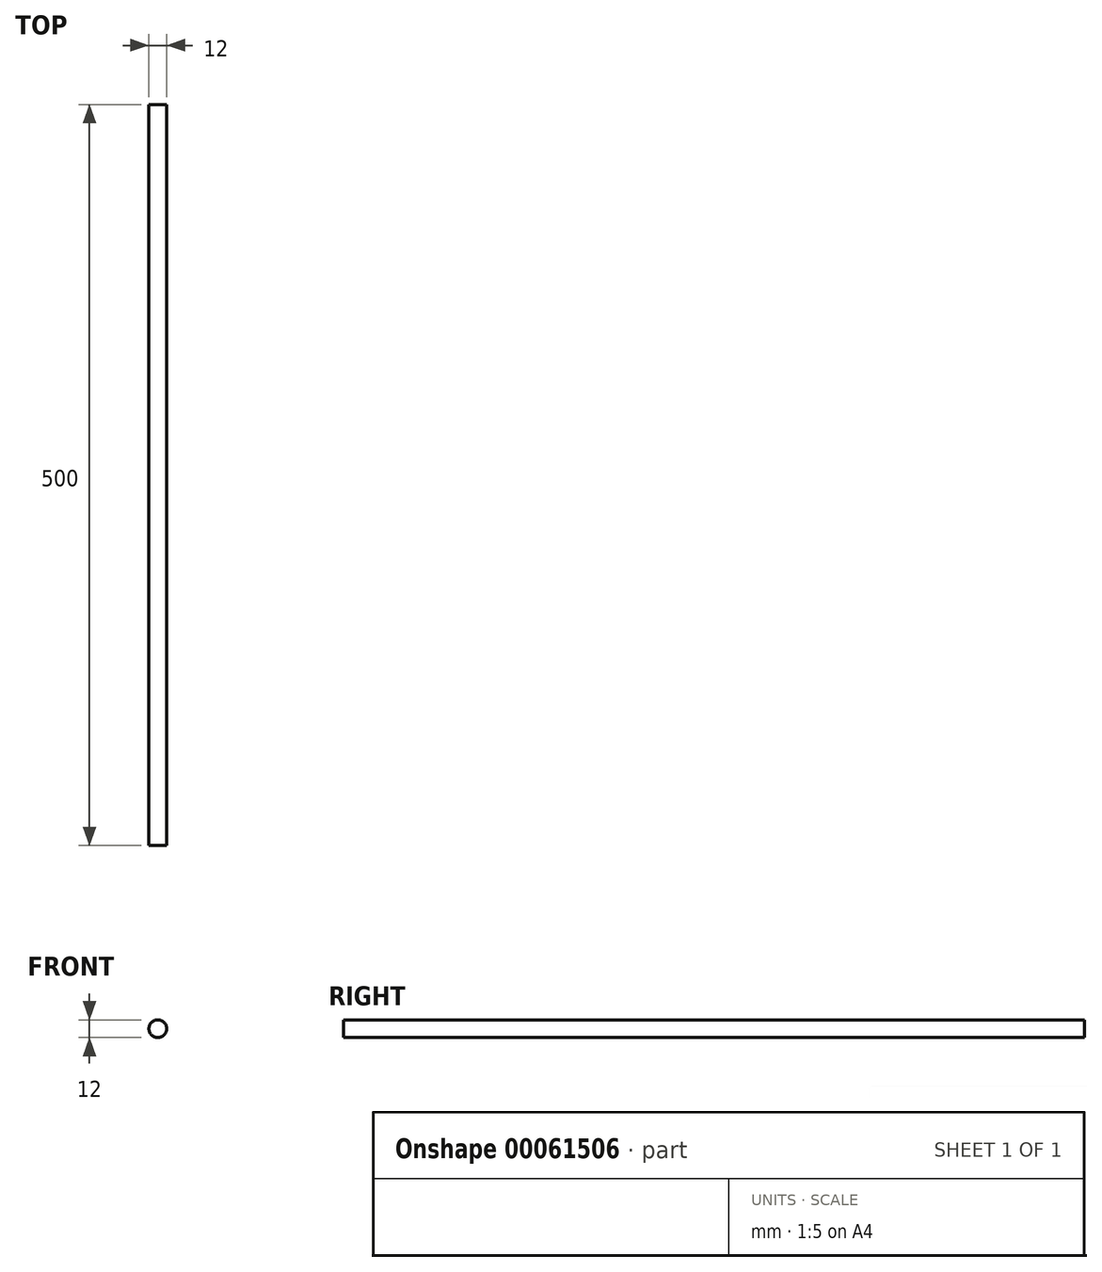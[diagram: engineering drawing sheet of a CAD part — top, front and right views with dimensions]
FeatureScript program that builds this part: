
annotation { "Feature Type Name" : "Feature", "Feature Type Description" : "" }
export const myFeature = defineFeature(function(context is Context, id is Id, definition is map)
    precondition{}
    {
        {
            var Q0;
            Q0=qCreatedBy(makeId("Front.planeOp"),FACE);
            var sketch = newSketch(context, id + "F0", { "sketchPlane" : qUnion([Q0])});
            skCircle(sketch, "E0", {"center": v(0, 0) * mm, "radius": 6 * mm});
            skSolve(sketch);
        }
        {
            var Q0;
            Q0=makeQuery(id+"F0.imprint","IMPRINT",FACE,{"disambiguationData":[TD([[makeQuery(id+"F0.imprint","IMPRINT",EDGE,{"derivedFrom":sQuery(id+"F0.wireOp",EDGE,"E0")}),1.0]])]});
            extrude(context, id + "F1", {"entities" : qUnion([Q0]), "depth" : 500 * mm, "symmetric" : true});
        }
    });
